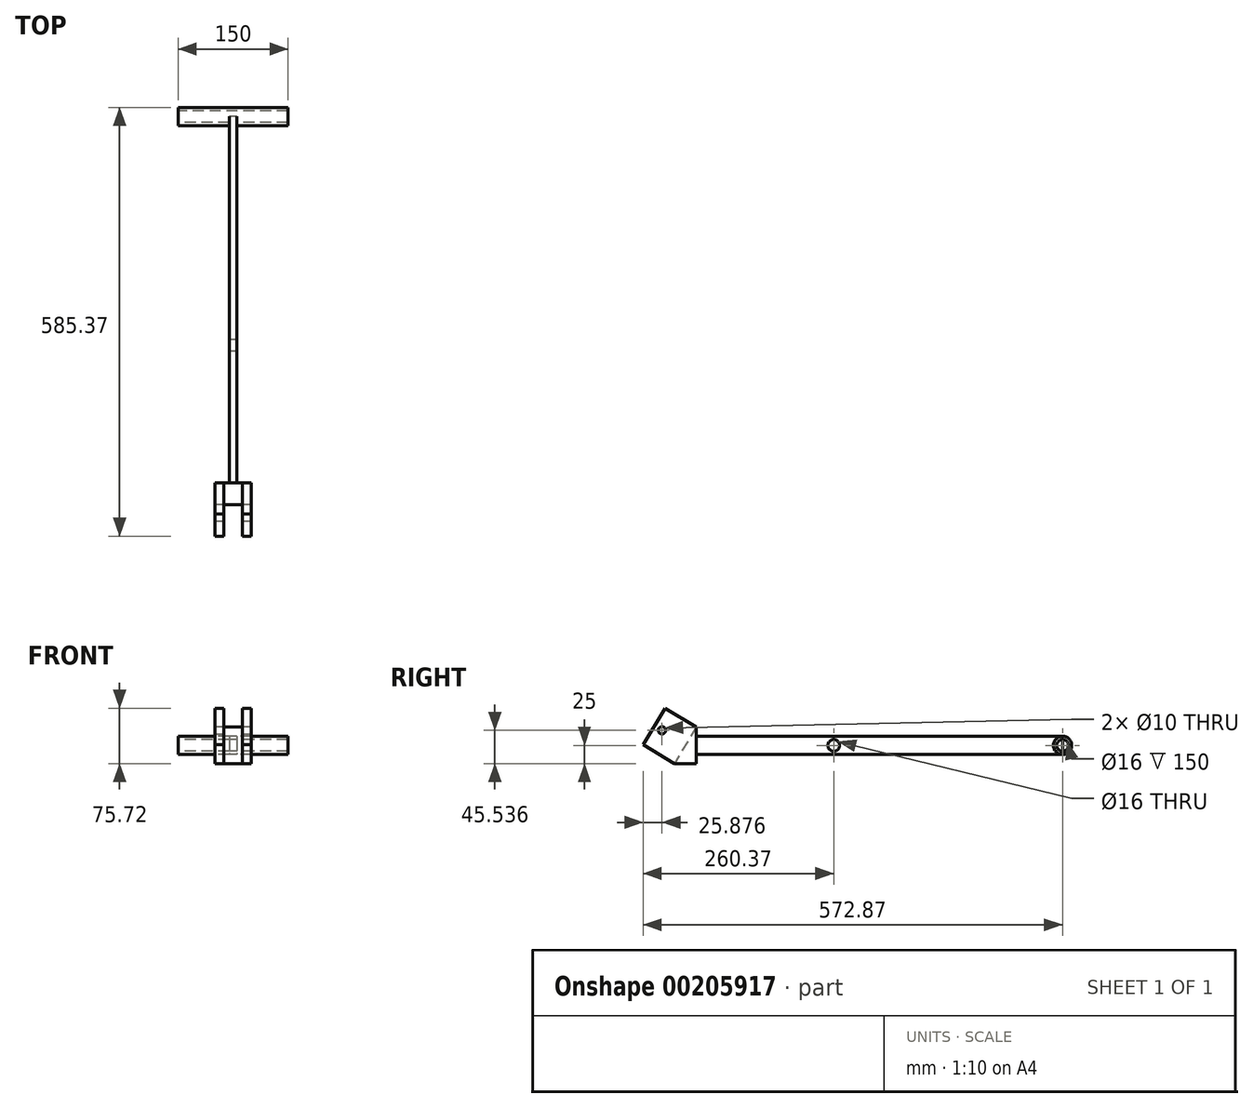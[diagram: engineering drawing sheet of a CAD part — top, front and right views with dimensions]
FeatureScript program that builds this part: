
annotation { "Feature Type Name" : "Feature", "Feature Type Description" : "" }
export const myFeature = defineFeature(function(context is Context, id is Id, definition is map)
    precondition{}
    {
        {
            var Q0;
            Q0=qCreatedBy(makeId("Right.planeOp"),FACE);
            var sketch = newSketch(context, id + "F0", { "sketchPlane" : qUnion([Q0])});
            skCircle(sketch, "E0", {"center": v(0, 0) * mm, "radius": 12.5 * mm});
            skCircle(sketch, "E1", {"center": v(0, 0) * mm, "radius": 8 * mm});
            skSolve(sketch);
        }
        {
            var Q0;
            Q0=makeQuery(id+"F0.imprint","IMPRINT",FACE,{"disambiguationData":[TD([[makeQuery(id+"F0.imprint","IMPRINT",EDGE,{"derivedFrom":sQuery(id+"F0.wireOp",EDGE,"E0")}),1.0]])]});
            extrude(context, id + "F1", {"entities" : qUnion([Q0]), "depth" : 75 * mm, "hasSecondDirection" : true, "secondDirectionOppositeDirection" : true, "secondDirectionDepth" : 75 * mm});
        }
        {
            var Q0;
            Q0=qCreatedBy(makeId("Right.planeOp"),FACE);
            var sketch = newSketch(context, id + "F2", { "sketchPlane" : qUnion([Q0])});
            skLineSegment(sketch, "E2.bottom", {"start": v(0, 12.5) * mm, "end": v(-500, 12.5) * mm});
            skLineSegment(sketch, "E2.top", {"start": v(0, -12.5) * mm, "end": v(-500, -12.5) * mm});
            skLineSegment(sketch, "E2.left", {"start": v(0, 12.5) * mm, "end": v(0, -12.5) * mm});
            skLineSegment(sketch, "E2.right", {"start": v(-500, 12.5) * mm, "end": v(-500, -12.5) * mm});
            skSolve(sketch);
        }
        {
            var Q0;
            Q0=makeQuery(id+"F2.imprint","IMPRINT",FACE,{"disambiguationData":[TD([[makeQuery(id+"F2.imprint","IMPRINT",EDGE,{"derivedFrom":sQuery(id+"F2.wireOp",EDGE,"E2.bottom")}),1.0]])]});
            extrude(context, id + "F3", {"entities" : qUnion([Q0]), "operationType" : NewBodyOperationType.ADD, "depth" : 5 * mm, "hasSecondDirection" : true, "secondDirectionOppositeDirection" : true, "secondDirectionDepth" : 5 * mm});
        }
        {
            var Q0;
            {var subQ0=sQuery(id+"F2.wireOp",EDGE,"E2.bottom");var subQ1=sQuery(id+"F2.wireOp",EDGE,"E2.top");var subQ2=sQuery(id+"F2.wireOp",EDGE,"E2.right");Q0=makeQuery(id+"F3.boolean.opBoolean","SPLIT",FACE,{"disambiguationData":[TD([makeQuery(id+"F1.opExtrude","SWEPT_FACE",FACE,{"disambiguationData":[OSD([sQuery(id+"F0.wireOp",EDGE,"E0")])]})])],"derivedFrom":makeQuery(id+"F3.opExtrude","CAP_FACE",FACE,{"disambiguationData":[OSD([subQ0,subQ1,sQuery(id+"F2.wireOp",EDGE,"E2.left"),subQ2])],"isStart":false})});}
            var sketch = newSketch(context, id + "F4", { "sketchPlane" : qUnion([Q0])});
            skCircle(sketch, "E3", {"center": v(-312.5, 0) * mm, "radius": 8 * mm});
            skSolve(sketch);
        }
        {
            var Q0;
            Q0=makeQuery(id+"F4.imprint","IMPRINT",FACE,{"disambiguationData":[TD([[makeQuery(id+"F4.imprint","IMPRINT",EDGE,{"derivedFrom":sQuery(id+"F4.wireOp",EDGE,"E3")}),1.0]])]});
            var Q1;
            Q1=sQuery(id+"F4.wireOp",EDGE,"E3");
            extrude(context, id + "F5", {"entities" : qUnion([Q0]), "operationType" : NewBodyOperationType.REMOVE, "surfaceEntities" : qUnion([Q1]), "depth" : 25 * mm, "hasSecondDirection" : true, "secondDirectionOppositeDirection" : true, "secondDirectionDepth" : 25 * mm});
        }
        {
            var Q0;
            Q0=makeQuery(id+"F3.opExtrude","SWEPT_FACE",FACE,{"disambiguationData":[OSD([sQuery(id+"F2.wireOp",EDGE,"E2.right")])]});
            var sketch = newSketch(context, id + "F6", { "sketchPlane" : qUnion([Q0])});
            skLineSegment(sketch, "E4.bottom", {"start": v(25, -25) * mm, "end": v(-25, -25) * mm});
            skLineSegment(sketch, "E4.top", {"start": v(25, 25) * mm, "end": v(-25, 25) * mm});
            skLineSegment(sketch, "E4.left", {"start": v(25, -25) * mm, "end": v(25, 25) * mm});
            skLineSegment(sketch, "E4.right", {"start": v(-25, -25) * mm, "end": v(-25, 25) * mm});
            skPoint(sketch, "E4.middle", {"position": v(0, 0) * mm});
            skSolve(sketch);
        }
        {
            var Q0;
            Q0=makeQuery(id+"F6.imprint","IMPRINT",FACE,{"disambiguationData":[TD([[makeQuery(id+"F6.imprint","IMPRINT",EDGE,{"derivedFrom":sQuery(id+"F6.wireOp",EDGE,"E4.bottom")}),-1.0]])]});
            var Q1;
            {var subQ0=sQuery(id+"F2.wireOp",EDGE,"E2.right");Q1=makeQuery(id+"F6.imprint","IMPRINT",FACE,{"disambiguationData":[TD([[makeQuery(id+"F6.imprint","IMPRINT",EDGE,{"derivedFrom":makeQuery(id+"F3.opExtrude","CAP_EDGE",EDGE,{"disambiguationData":[OSD([subQ0])],"isStart":true})}),1.0]])]});}
            extrude(context, id + "F7", {"entities" : qUnion([Q0, Q1]), "operationType" : NewBodyOperationType.ADD, "depth" : 30 * mm});
        }
        {
            var Q0;
            Q0=makeQuery(id+"F7.opExtrude","SWEPT_FACE",FACE,{"disambiguationData":[OSD([sQuery(id+"F6.wireOp",EDGE,"E4.left")])]});
            var sketch = newSketch(context, id + "F8", { "sketchPlane" : qUnion([Q0])});
            skLineSegment(sketch, "E5", {"start": v(-530, -25) * mm, "end": v(-500, 25) * mm});
            skLineSegment(sketch, "E6", {"start": v(-500, 25) * mm, "end": v(-530, 25) * mm});
            skLineSegment(sketch, "E7", {"start": v(-530, 25) * mm, "end": v(-530, -25) * mm});
            skLineSegment(sketch, "E8", {"start": v(-530, -25) * mm, "end": v(-530, -25) * mm});
            skSolve(sketch);
        }
        {
            var Q0;
            Q0=makeQuery(id+"F8.imprint","IMPRINT",FACE,{"disambiguationData":[TD([[makeQuery(id+"F8.imprint","IMPRINT",EDGE,{"derivedFrom":sQuery(id+"F8.wireOp",EDGE,"E5")}),1.0]])]});
            extrude(context, id + "F9", {"entities" : qUnion([Q0]), "operationType" : NewBodyOperationType.REMOVE, "oppositeDirection" : true, "depth" : 50 * mm});
        }
        {
            var Q0;
            Q0=makeQuery(id+"F9.boolean.opBoolean","COPY",FACE,{"derivedFrom":makeQuery(id+"F9.opExtrude","SWEPT_FACE",FACE,{"disambiguationData":[OSD([sQuery(id+"F8.wireOp",EDGE,"E5")])]})});
            var sketch = newSketch(context, id + "F10", { "sketchPlane" : qUnion([Q0])});
            skLineSegment(sketch, "E9.bottom", {"start": v(-25, -235.81) * mm, "end": v(-12.5, -235.81) * mm});
            skLineSegment(sketch, "E9.top", {"start": v(-25, -294.12) * mm, "end": v(-12.5, -294.12) * mm});
            skLineSegment(sketch, "E9.left", {"start": v(-25, -235.81) * mm, "end": v(-25, -294.12) * mm});
            skLineSegment(sketch, "E9.right", {"start": v(-12.5, -235.81) * mm, "end": v(-12.5, -294.12) * mm});
            skLineSegment(sketch, "E10.bottom", {"start": v(25, -235.81) * mm, "end": v(12.5, -235.81) * mm});
            skLineSegment(sketch, "E10.top", {"start": v(25, -294.12) * mm, "end": v(12.5, -294.12) * mm});
            skLineSegment(sketch, "E10.left", {"start": v(25, -235.81) * mm, "end": v(25, -294.12) * mm});
            skLineSegment(sketch, "E10.right", {"start": v(12.5, -235.81) * mm, "end": v(12.5, -294.12) * mm});
            skSolve(sketch);
        }
        {
            var Q0;
            Q0=makeQuery(id+"F10.imprint","IMPRINT",FACE,{"disambiguationData":[TD([[makeQuery(id+"F10.imprint","IMPRINT",EDGE,{"derivedFrom":sQuery(id+"F10.wireOp",EDGE,"E9.bottom")}),1.0]])]});
            var Q1;
            Q1=makeQuery(id+"F10.imprint","IMPRINT",FACE,{"disambiguationData":[TD([[makeQuery(id+"F10.imprint","IMPRINT",EDGE,{"derivedFrom":sQuery(id+"F10.wireOp",EDGE,"E10.bottom")}),1.0]])]});
            extrude(context, id + "F11", {"entities" : qUnion([Q0, Q1]), "operationType" : NewBodyOperationType.ADD, "depth" : 50 * mm});
        }
        {
            var Q0;
            Q0=makeQuery(id+"F11.boolean.opBoolean","MERGE",FACE,{"derivedFrom":[makeQuery(id+"F7.opExtrude","SWEPT_FACE",FACE,{"disambiguationData":[OSD([sQuery(id+"F6.wireOp",EDGE,"E4.left")])]}),makeQuery(id+"F11.opExtrude","SWEPT_FACE",FACE,{"disambiguationData":[OSD([sQuery(id+"F10.wireOp",EDGE,"E10.left")])]})]});
            var sketch = newSketch(context, id + "F12", { "sketchPlane" : qUnion([Q0])});
            skCircle(sketch, "E11", {"center": v(-547, 20.54) * mm, "radius": 5 * mm});
            skSolve(sketch);
        }
        {
            var Q0;
            Q0=makeQuery(id+"F12.imprint","IMPRINT",FACE,{"disambiguationData":[TD([[makeQuery(id+"F12.imprint","IMPRINT",EDGE,{"derivedFrom":sQuery(id+"F12.wireOp",EDGE,"E11")}),1.0]])]});
            extrude(context, id + "F13", {"entities" : qUnion([Q0]), "operationType" : NewBodyOperationType.REMOVE, "endBound" : BoundingType.THROUGH_ALL, "oppositeDirection" : true, "depth" : 25 * mm});
        }
    });
